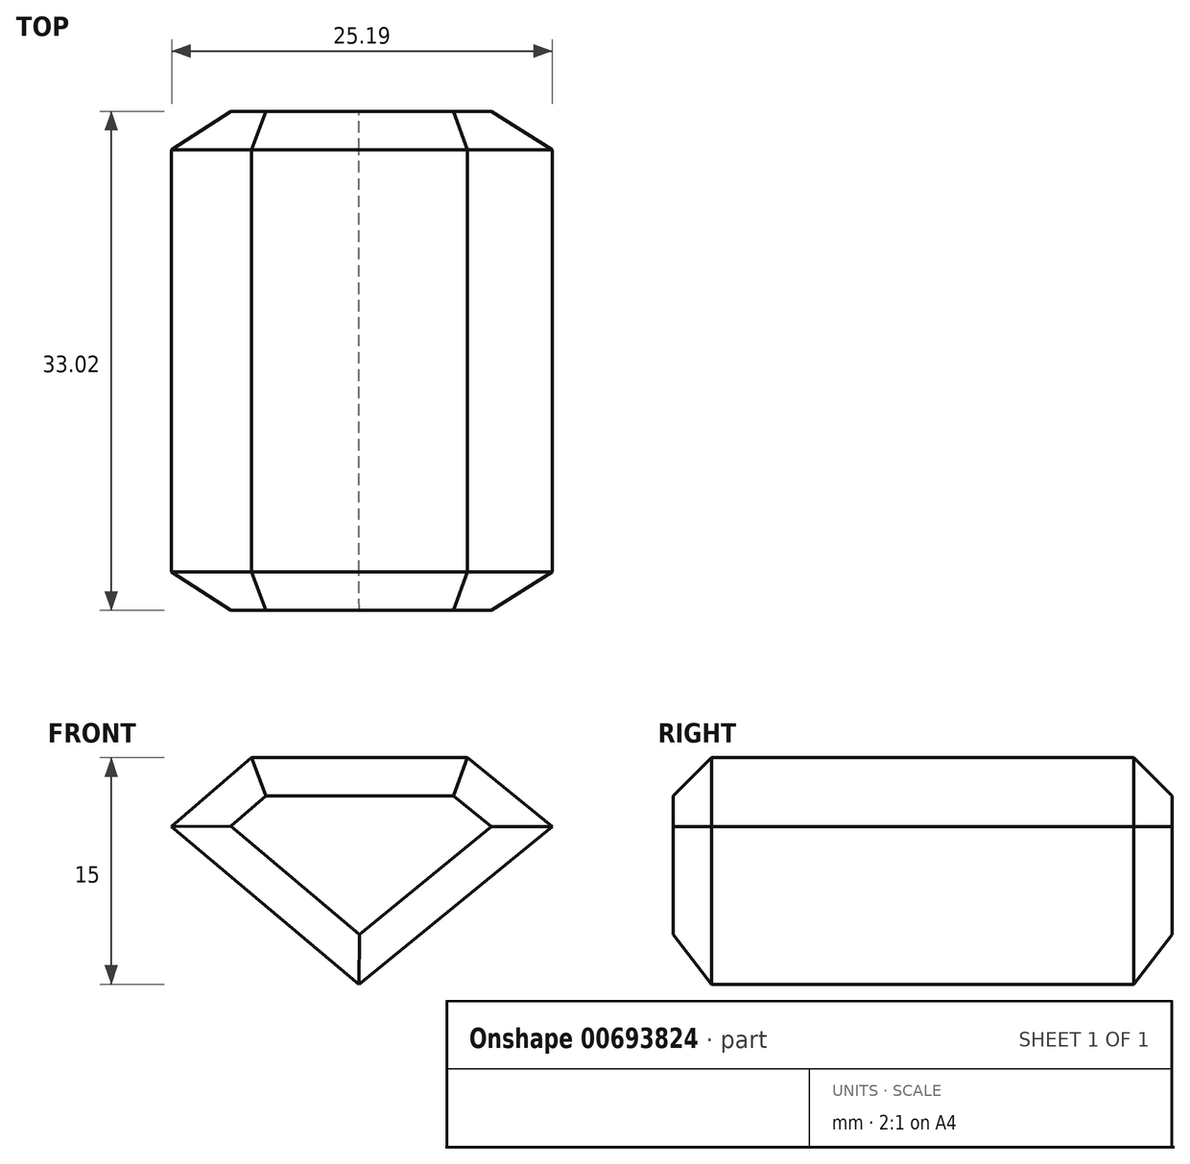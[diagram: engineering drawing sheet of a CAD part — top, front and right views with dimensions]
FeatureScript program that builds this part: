
annotation { "Feature Type Name" : "Feature", "Feature Type Description" : "" }
export const myFeature = defineFeature(function(context is Context, id is Id, definition is map)
    precondition{}
    {
        {
            var Q0;
            Q0=qCreatedBy(makeId("Front.planeOp"),FACE);
            var sketch = newSketch(context, id + "F0", { "sketchPlane" : qUnion([Q0])});
            skLineSegment(sketch, "E0", {"start": v(3.77, -9.2) * mm, "end": v(-8.62, 1.23) * mm});
            skLineSegment(sketch, "E1", {"start": v(-8.62, 1.23) * mm, "end": v(-3.33, 5.8) * mm});
            skLineSegment(sketch, "E2", {"start": v(-3.33, 5.8) * mm, "end": v(10.94, 5.8) * mm});
            skLineSegment(sketch, "E3", {"start": v(10.94, 5.8) * mm, "end": v(16.57, 1.23) * mm});
            skLineSegment(sketch, "E4", {"start": v(16.57, 1.23) * mm, "end": v(3.77, -9.2) * mm});
            skSolve(sketch);
        }
        {
            var Q0;
            Q0=makeQuery(id+"F0.imprint","IMPRINT",FACE,{"disambiguationData":[TD([[makeQuery(id+"F0.imprint","IMPRINT",EDGE,{"derivedFrom":sQuery(id+"F0.wireOp",EDGE,"E0")}),-1.0]])]});
            extrude(context, id + "F1", {"entities" : qUnion([Q0]), "depth" : 27.94 * mm, "offsetDistance" : 25.4 * mm});
        }
        {
            var Q0;
            Q0=makeQuery(id+"F1.opExtrude","CAP_EDGE",EDGE,{"disambiguationData":[OSD([sQuery(id+"F0.wireOp",EDGE,"E4")])],"isStart":false});
            chamfer(context, id + "F2", {"entities" : qUnion([Q0]), "width" : 2.54 * mm, "tangentPropagation" : true});
        }
        {
            var Q0;
            Q0=makeQuery(id+"F1.opExtrude","CAP_EDGE",EDGE,{"disambiguationData":[OSD([sQuery(id+"F0.wireOp",EDGE,"E0")])],"isStart":false});
            var Q1;
            Q1=makeQuery(id+"F1.opExtrude","CAP_EDGE",EDGE,{"disambiguationData":[OSD([sQuery(id+"F0.wireOp",EDGE,"E1")])],"isStart":false});
            var Q2;
            Q2=makeQuery(id+"F1.opExtrude","CAP_EDGE",EDGE,{"disambiguationData":[OSD([sQuery(id+"F0.wireOp",EDGE,"E2")])],"isStart":false});
            var Q3;
            Q3=makeQuery(id+"F1.opExtrude","CAP_EDGE",EDGE,{"disambiguationData":[OSD([sQuery(id+"F0.wireOp",EDGE,"E3")])],"isStart":false});
            chamfer(context, id + "F3", {"entities" : qUnion([Q0, Q1, Q2, Q3]), "width" : 2.54 * mm, "tangentPropagation" : true});
        }
        {
            var Q0;
            Q0=makeQuery(id+"F1.opExtrude","CAP_FACE",FACE,{"disambiguationData":[OSD([sQuery(id+"F0.wireOp",EDGE,"E0"),sQuery(id+"F0.wireOp",EDGE,"E1"),sQuery(id+"F0.wireOp",EDGE,"E2"),sQuery(id+"F0.wireOp",EDGE,"E3"),sQuery(id+"F0.wireOp",EDGE,"E4")])],"isStart":true});
            extrude(context, id + "F4", {"entities" : qUnion([Q0]), "operationType" : NewBodyOperationType.ADD, "depth" : 5.08 * mm, "offsetDistance" : 25.4 * mm});
        }
        {
            var Q0;
            Q0=makeQuery(id+"F4.opExtrude","CAP_FACE",FACE,{"disambiguationData":[OSD([sQuery(id+"F0.wireOp",EDGE,"E0"),sQuery(id+"F0.wireOp",EDGE,"E1"),sQuery(id+"F0.wireOp",EDGE,"E2"),sQuery(id+"F0.wireOp",EDGE,"E3"),sQuery(id+"F0.wireOp",EDGE,"E4")])],"isStart":false});
            chamfer(context, id + "F5", {"entities" : qUnion([Q0]), "width" : 2.54 * mm, "tangentPropagation" : true});
        }
    });
